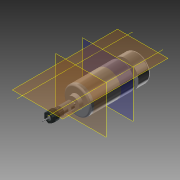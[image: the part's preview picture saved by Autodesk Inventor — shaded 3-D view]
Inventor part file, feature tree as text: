
AUTODESK INVENTOR PART (.ipt)
format: ipt  version: 2013 (Build 170138000, 138)  size: 302,080 bytes
history: native  units: mm
features: extrude x16, sketch x16, other x13, fillet x3, chamfer x2, projected_geometry x1
ambient origin geometry x8: Origin, YZ Plane, XZ Plane, XY Plane, X Axis, Y Axis, Z Axis, Center Point
feature tree (51):
  other  "Těleso1"
  extrude  "Vysunutí1"  Depth=26.0mm
  extrude  "Vysunutí2"  Depth=90.0mm TaperAngle=0.0deg
  fillet  "Zaoblení1"  Radius=13.0mm
  fillet  "Zaoblení2"  Radius=7.0mm
  extrude  "Vysunutí3"  Depth=3.0mm
  chamfer  "Zkosení1"  Distance=3.0mm
  extrude  "Vysunutí4"  Depth=4.0mm
  extrude  "Vysunutí5"  Depth=5.0mm TaperAngle=0.0deg
  extrude  "Vysunutí6"  Depth=7.0mm
  extrude  "Vysunutí7"  Depth=8.0mm
  extrude  "Vysunutí8"  Depth=44.0mm TaperAngle=0.0deg
  extrude  "Vysunutí9"  Depth=9.5mm
  chamfer  "Zkosení2"  Distance=13.0mm
  other  "Pracovní rovina1"
  extrude  "Vysunutí10"  Depth=5.0mm
  other  "Závit1"
  extrude  "Vysunutí11"  Depth=3.0mm TaperAngle=0.0deg
  extrude  "Vysunutí12"  Depth=5.0mm TaperAngle=0.0deg
  fillet  "Zaoblení3"  Radius=3.175mm
  extrude  "Vysunutí13"  Depth=5.0mm TaperAngle=0.0deg
  other  "Pracovní rovina2"
  extrude  "Vysunutí14"  Depth=2.0mm
  other  "Pracovní rovina5"
  other  "Pracovní rovina4"
  extrude  "Vysunutí15"  Depth=10.0mm TaperAngle=0.0deg
  other  "Pracovní rovina6"
  extrude  "Vysunutí16"  Depth=0.52mm
  other  "Pracovní rovina7"
  sketch  "Náčrt2"
  sketch  "Náčrt3"
  sketch  "Náčrt4"
  sketch  "Náčrt5"
  sketch  "Náčrt6"
  sketch  "Náčrt7"
  sketch  "Náčrt8"
  sketch  "Náčrt9"
  sketch  "Náčrt10"
  sketch  "Náčrt11"
  sketch  "Náčrt12"
  sketch  "Náčrt13"
  sketch  "Náčrt14"
  sketch  "Náčrt15"
  other  "Těleso2"
  sketch  "Náčrt17"
  other  "Těleso3"
  sketch  "Náčrt18"
  projected_geometry  "Promítnutá smyčka1"
  other  "Těleso4"
  other  "Pracovní osa1"
  other  "Pracovní osa2"
